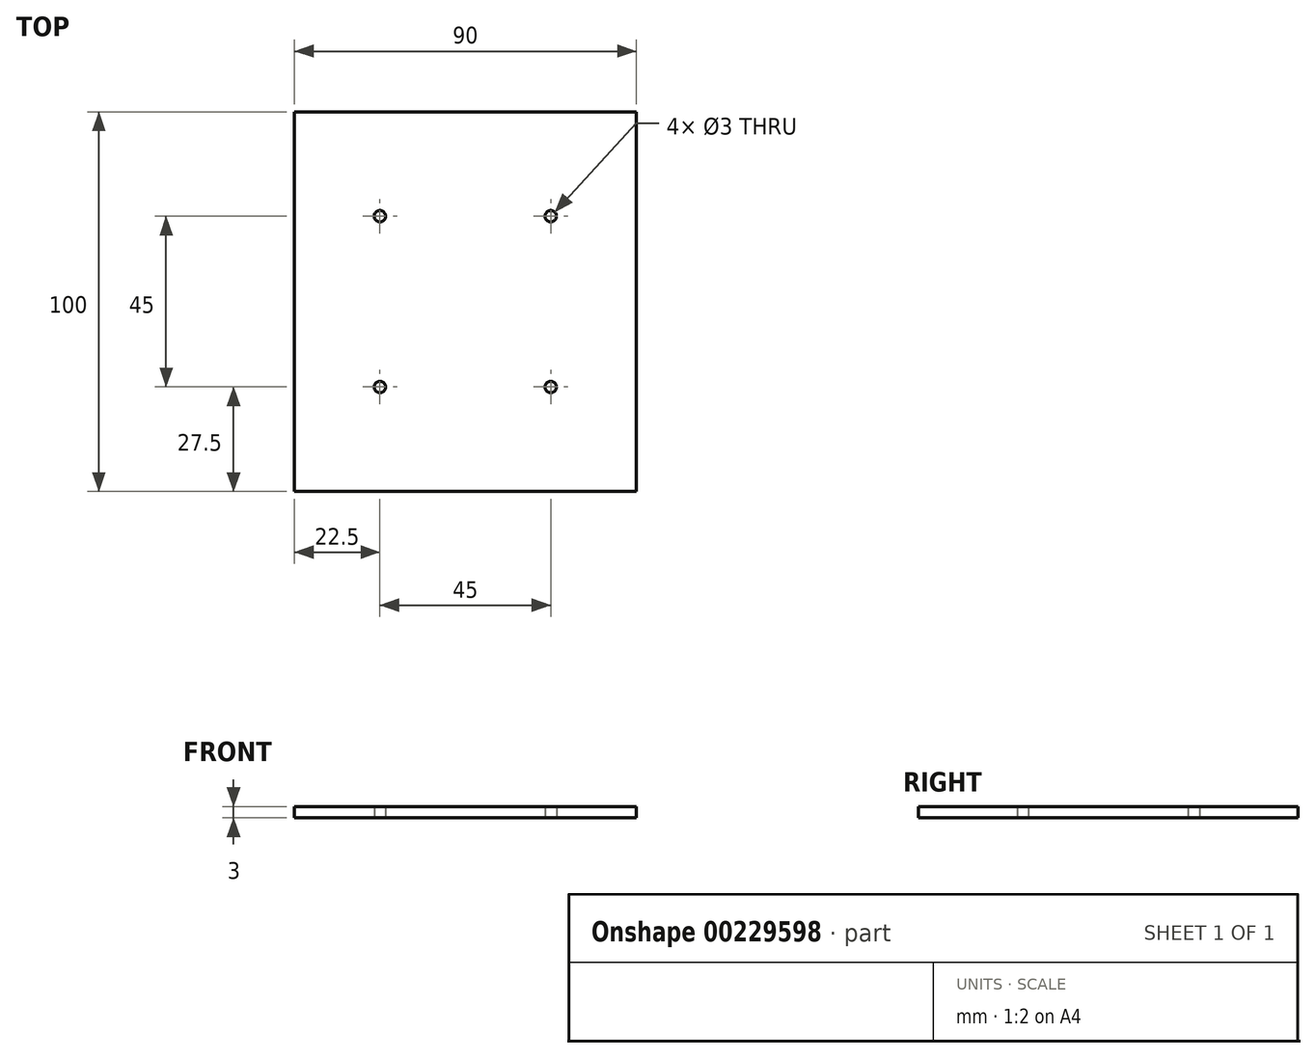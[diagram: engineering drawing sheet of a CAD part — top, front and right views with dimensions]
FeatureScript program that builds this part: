
annotation { "Feature Type Name" : "Feature", "Feature Type Description" : "" }
export const myFeature = defineFeature(function(context is Context, id is Id, definition is map)
    precondition{}
    {
        {
            var Q0;
            Q0=qCreatedBy(makeId("Top.planeOp"),FACE);
            var sketch = newSketch(context, id + "F0", { "sketchPlane" : qUnion([Q0])});
            skLineSegment(sketch, "E0.bottom", {"start": v(45, -50) * mm, "end": v(-45, -50) * mm});
            skLineSegment(sketch, "E0.top", {"start": v(45, 50) * mm, "end": v(-45, 50) * mm});
            skLineSegment(sketch, "E0.left", {"start": v(45, -50) * mm, "end": v(45, 50) * mm});
            skLineSegment(sketch, "E0.right", {"start": v(-45, -50) * mm, "end": v(-45, 50) * mm});
            skPoint(sketch, "E0.middle", {"position": v(0, 0) * mm});
            skCircle(sketch, "E1", {"center": v(-22.5, 22.5) * mm, "radius": 1.5 * mm});
            skCircle(sketch, "E2.MirrorC", {"center": v(22.5, 22.5) * mm, "radius": 1.5 * mm});
            skCircle(sketch, "E3.MirrorC", {"center": v(22.5, -22.5) * mm, "radius": 1.5 * mm});
            skCircle(sketch, "E4.MirrorC", {"center": v(-22.5, -22.5) * mm, "radius": 1.5 * mm});
            skSolve(sketch);
        }
        {
            var Q0;
            Q0=makeQuery(id+"F0.imprint","IMPRINT",FACE,{"disambiguationData":[TD([[makeQuery(id+"F0.imprint","IMPRINT",EDGE,{"derivedFrom":sQuery(id+"F0.wireOp",EDGE,"E0.bottom")}),-1.0]])]});
            extrude(context, id + "F1", {"entities" : qUnion([Q0]), "depth" : 3 * mm});
        }
    });
